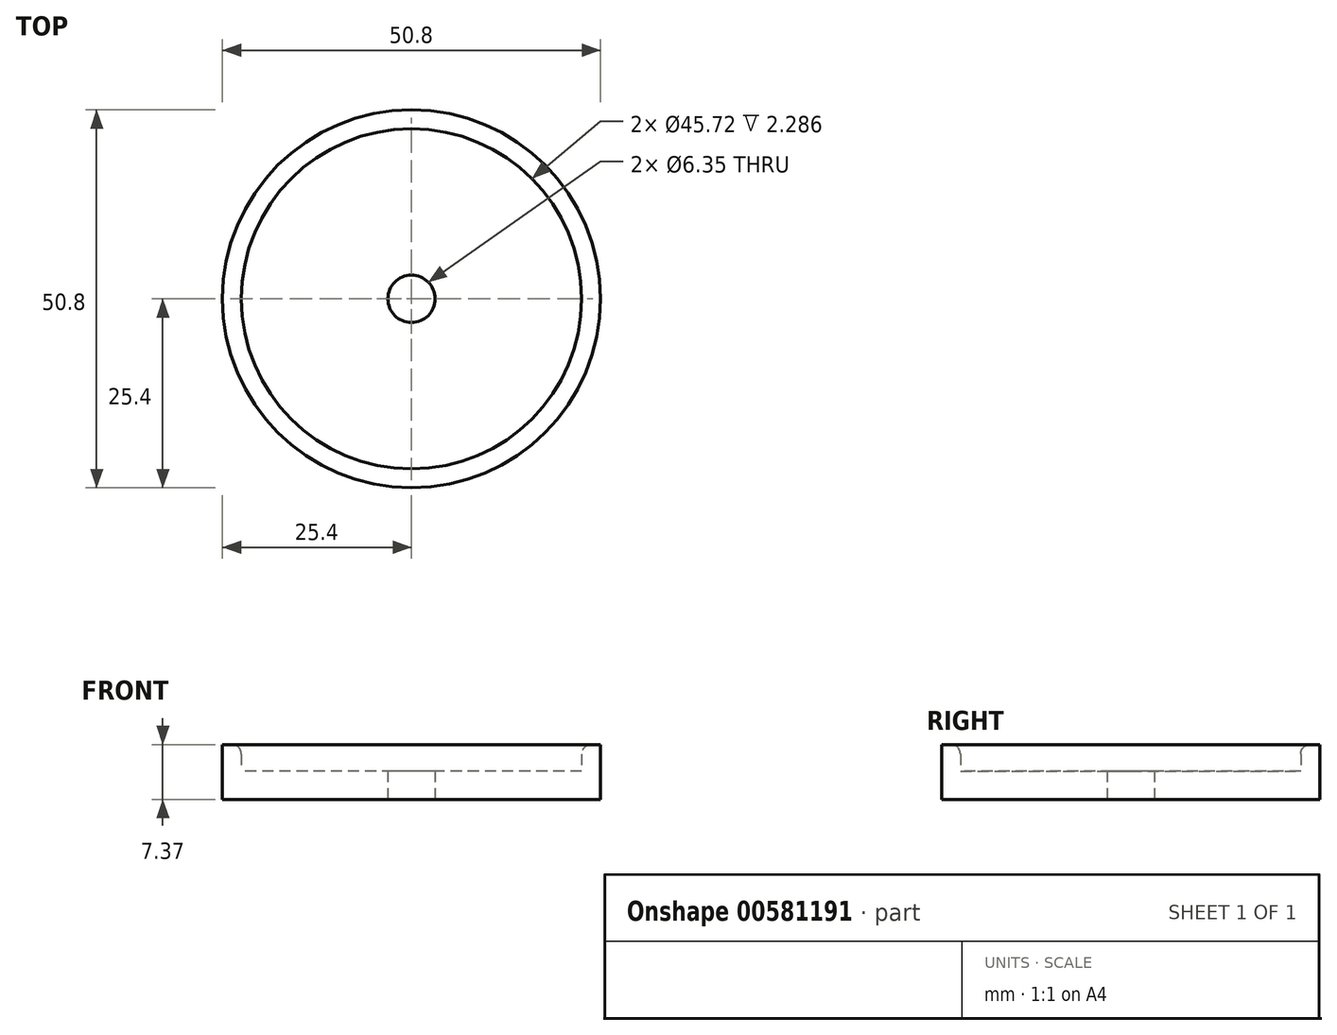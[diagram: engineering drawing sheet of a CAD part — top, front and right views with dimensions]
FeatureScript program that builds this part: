
annotation { "Feature Type Name" : "Feature", "Feature Type Description" : "" }
export const myFeature = defineFeature(function(context is Context, id is Id, definition is map)
    precondition{}
    {
        {
            var Q0;
            Q0=qCreatedBy(makeId("Top.planeOp"),FACE);
            var sketch = newSketch(context, id + "F0", { "sketchPlane" : qUnion([Q0])});
            skCircle(sketch, "E0", {"center": v(0, 0) * mm, "radius": 25.4 * mm});
            skSolve(sketch);
        }
        {
            var Q0;
            Q0=makeQuery(id+"F0.imprint","IMPRINT",FACE,{"disambiguationData":[TD([[makeQuery(id+"F0.imprint","IMPRINT",EDGE,{"derivedFrom":sQuery(id+"F0.wireOp",EDGE,"E0")}),1.0]])]});
            extrude(context, id + "F1", {"entities" : qUnion([Q0]), "depth" : 3.8 * mm, "offsetDistance" : 25.4 * mm});
        }
        {
            var Q0;
            Q0=makeQuery(id+"F1.opExtrude","CAP_FACE",FACE,{"disambiguationData":[OSD([sQuery(id+"F0.wireOp",EDGE,"E0")])],"isStart":false});
            var sketch = newSketch(context, id + "F2", { "sketchPlane" : qUnion([Q0])});
            skCircle(sketch, "E1", {"center": v(0, 0) * mm, "radius": 25.4 * mm});
            skCircle(sketch, "E2.0", {"center": v(0, 0) * mm, "radius": 22.86 * mm});
            skSolve(sketch);
        }
        {
            var Q0;
            Q0 = qSketchRegion(id + "F2", true);
            extrude(context, id + "F3", {"entities" : qUnion([Q0]), "operationType" : NewBodyOperationType.ADD, "depth" : 3.56 * mm, "offsetDistance" : 25.4 * mm});
        }
        {
            var Q0;
            Q0=makeQuery(id+"F3.opExtrude","CAP_EDGE",EDGE,{"disambiguationData":[OSD([sQuery(id+"F2.wireOp",EDGE,"E2.0")])],"isStart":false});
            var Q1;
            Q1=makeQuery(id+"F3.opExtrude","CAP_EDGE",EDGE,{"disambiguationData":[OSD([sQuery(id+"F2.wireOp",EDGE,"E2.0")])],"isStart":true});
            fillet(context, id + "F4", {"entities" : qUnion([Q0, Q1]), "radius" : 1.27 * mm, "tangentPropagation" : true, "allowEdgeOverflow" : false});
        }
        {
            var Q0;
            Q0=qCreatedBy(makeId("Top.planeOp"),FACE);
            var sketch = newSketch(context, id + "F5", { "sketchPlane" : qUnion([Q0])});
            skCircle(sketch, "E3", {"center": v(0, 0) * mm, "radius": 3.17 * mm});
            skSolve(sketch);
        }
        {
            var Q0;
            Q0 = qSketchRegion(id + "F5", true);
            extrude(context, id + "F6", {"entities" : qUnion([Q0]), "operationType" : NewBodyOperationType.REMOVE, "endBound" : BoundingType.THROUGH_ALL, "depth" : 25.4 * mm, "offsetDistance" : 25.4 * mm});
        }
        {
            var Q0;
            Q0=makeQuery(id+"F1.opExtrude","SWEPT_BODY",BODY,{"disambiguationData":[OSD([sQuery(id+"F0.wireOp",EDGE,"E0")])]});
            transform(context, id + "F7", {"entities" : qUnion([Q0]), "transformType" : TransformType.TRANSLATION_3D, "dx" : 0 * mm, "dy" : 0 * mm, "dz" : 0 * mm, "makeCopy" : true});
        }
    });
